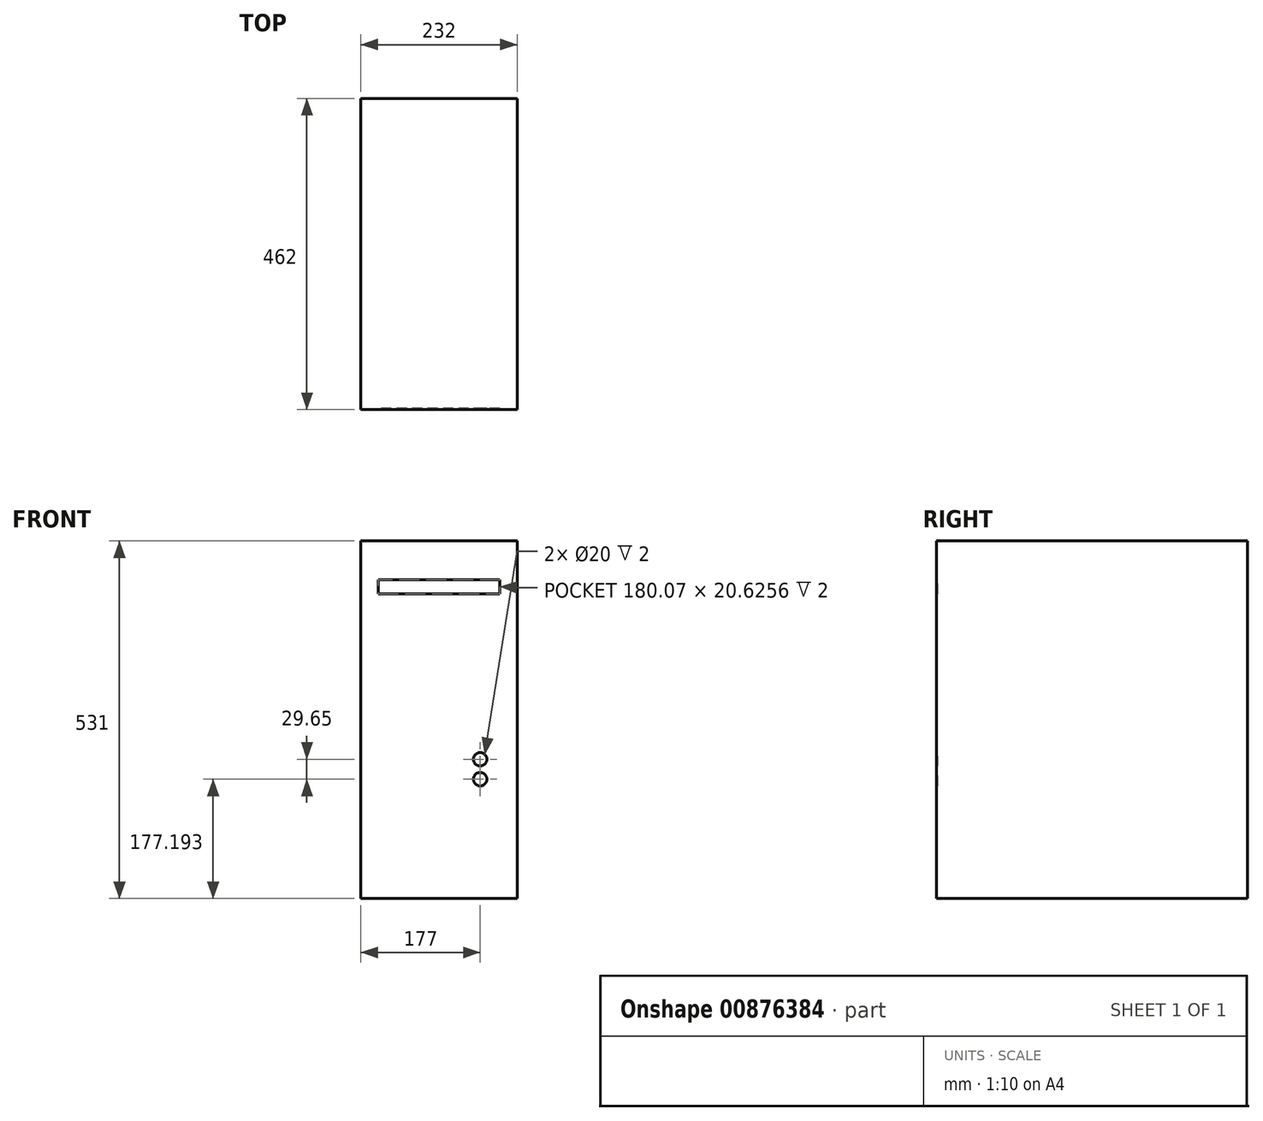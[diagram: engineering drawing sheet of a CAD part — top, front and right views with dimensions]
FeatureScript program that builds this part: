
annotation { "Feature Type Name" : "Feature", "Feature Type Description" : "" }
export const myFeature = defineFeature(function(context is Context, id is Id, definition is map)
    precondition{}
    {
        {
            var Q0;
            Q0=qCreatedBy(makeId("Front.planeOp"),FACE);
            var sketch = newSketch(context, id + "F0", { "sketchPlane" : qUnion([Q0])});
            skLineSegment(sketch, "E0.bottom", {"start": v(0, 0) * mm, "end": v(232, 0) * mm});
            skLineSegment(sketch, "E0.top", {"start": v(0, 531) * mm, "end": v(232, 531) * mm});
            skLineSegment(sketch, "E0.left", {"start": v(0, 0) * mm, "end": v(0, 531) * mm});
            skLineSegment(sketch, "E0.right", {"start": v(232, 0) * mm, "end": v(232, 531) * mm});
            skSolve(sketch);
        }
        {
            var Q0;
            Q0 = qSketchRegion(id + "F0", true);
            extrude(context, id + "F1", {"entities" : qUnion([Q0]), "depth" : 462 * mm, "offsetDistance" : 25 * mm});
        }
        {
            var Q0;
            Q0=makeQuery(id+"F1.opExtrude","CAP_FACE",FACE,{"disambiguationData":[OSD([sQuery(id+"F0.wireOp",EDGE,"E0.bottom"),sQuery(id+"F0.wireOp",EDGE,"E0.top"),sQuery(id+"F0.wireOp",EDGE,"E0.left"),sQuery(id+"F0.wireOp",EDGE,"E0.right")])],"isStart":false});
            var sketch = newSketch(context, id + "F2", { "sketchPlane" : qUnion([Q0])});
            skLineSegment(sketch, "E1.bottom", {"start": v(206.03, 452.53) * mm, "end": v(25.97, 452.53) * mm});
            skLineSegment(sketch, "E1.top", {"start": v(206.03, 473.16) * mm, "end": v(25.97, 473.16) * mm});
            skLineSegment(sketch, "E1.left", {"start": v(206.03, 452.53) * mm, "end": v(206.03, 473.16) * mm});
            skLineSegment(sketch, "E1.right", {"start": v(25.97, 452.53) * mm, "end": v(25.97, 473.16) * mm});
            skPoint(sketch, "E1.middle", {"position": v(116, 462.85) * mm});
            skPoint(sketch, "E1.middle.positionSnap0", {"position": v(116, 531) * mm});
            skPoint(sketch, "E1.centerSnap0", {"position": v(116, 531) * mm});
            skCircle(sketch, "E2", {"center": v(177, 206.84) * mm, "radius": 10 * mm});
            skCircle(sketch, "E3", {"center": v(177, 177.2) * mm, "radius": 10 * mm});
            skSolve(sketch);
        }
        {
            var Q0;
            Q0 = qSketchRegion(id + "F2", true);
            extrude(context, id + "F3", {"entities" : qUnion([Q0]), "operationType" : NewBodyOperationType.REMOVE, "oppositeDirection" : true, "depth" : 2 * mm, "offsetDistance" : 25 * mm});
        }
    });
